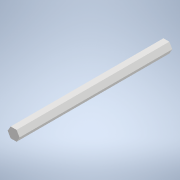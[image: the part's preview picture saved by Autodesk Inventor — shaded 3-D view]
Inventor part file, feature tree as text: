
AUTODESK INVENTOR PART (.ipt)
format: ipt  version: 2022 (Build 260153000, 153)  size: 118,784 bytes
history: native  units: mm
features: other x5, reference x4, extrude x2, sketch x2
ambient origin geometry x8: Origin, YZ Plane, XZ Plane, XY Plane, X Axis, Y Axis, Z Axis, Center Point
bodies: Solid1 (feature_tree)
feature tree (13):
  extrude  "Extrusion1"  Depth=3.1mm TaperAngle=360.0deg
  extrude  "Extrusion2"  Depth=10.0mm
  sketch  "Sketch1"  dims[d0=3.1mm d1=60.0mm d3=360.0deg]
  reference  "Reference1"
  reference  "Reference2"
  sketch  "Sketch2"  dims[d5=80.0mm d6=0.0mm d7=1.3mm d8=56.1mm d9=3.0mm d10=10.0mm d11=0.0mm]
  reference  "Reference3"
  reference  "Reference4"
  other  "<userpath>\OneDrive\Escritorio\Mini_Proyecto_Diseno\Diseno_18012\Modelo_MPD\caja_nuevo.iam"
  other  "caja_nuevo.iam"
  other  "Rodamiento_Ejes:2"
  other  "caja_2_Lateral:2"
  other  "hombro_nuevo:3"
